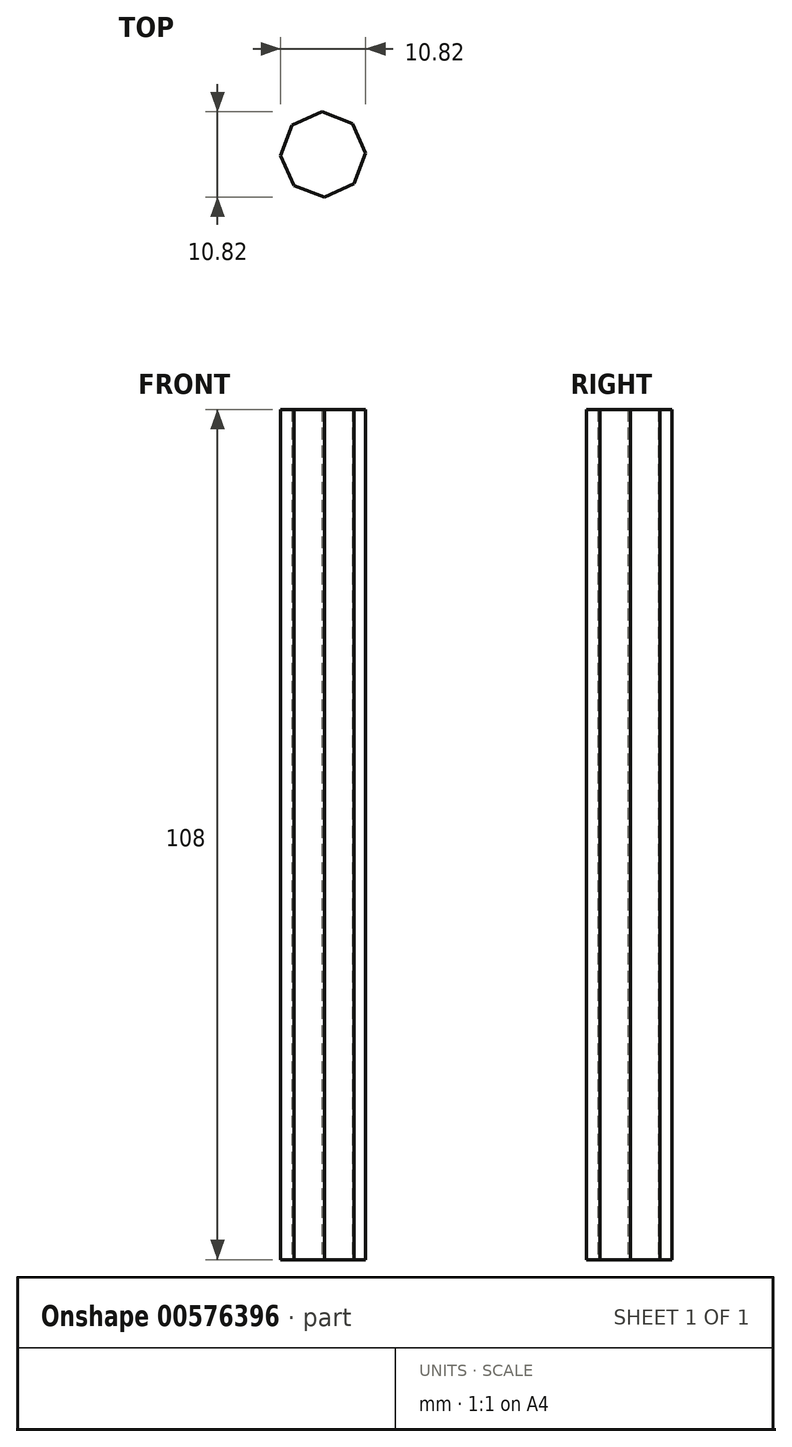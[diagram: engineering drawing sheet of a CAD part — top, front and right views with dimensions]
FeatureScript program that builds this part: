
annotation { "Feature Type Name" : "Feature", "Feature Type Description" : "" }
export const myFeature = defineFeature(function(context is Context, id is Id, definition is map)
    precondition{}
    {
        {
            var Q0;
            Q0=qCreatedBy(makeId("Top.planeOp"),FACE);
            var sketch = newSketch(context, id + "F0", { "sketchPlane" : qUnion([Q0])});
            skCircle(sketch, "E0.cCircle", {"center": v(0, 0) * mm, "radius": 5 * mm, "construction": true});
            skLineSegment(sketch, "E0.0", {"start": v(3.72, 3.93) * mm, "end": v(5.4, 0.15) * mm});
            skLineSegment(sketch, "E0.1", {"start": v(5.4, 0.15) * mm, "end": v(3.93, -3.72) * mm});
            skLineSegment(sketch, "E0.2", {"start": v(3.93, -3.72) * mm, "end": v(0.15, -5.4) * mm});
            skLineSegment(sketch, "E0.3", {"start": v(0.15, -5.4) * mm, "end": v(-3.72, -3.93) * mm});
            skLineSegment(sketch, "E0.4", {"start": v(-3.72, -3.93) * mm, "end": v(-5.4, -0.15) * mm});
            skLineSegment(sketch, "E0.5", {"start": v(-5.4, -0.15) * mm, "end": v(-3.93, 3.72) * mm});
            skLineSegment(sketch, "E0.6", {"start": v(-3.93, 3.72) * mm, "end": v(-0.15, 5.4) * mm});
            skLineSegment(sketch, "E0.7", {"start": v(-0.15, 5.4) * mm, "end": v(3.72, 3.93) * mm});
            skPoint(sketch, "E0.0.midPoint", {"position": v(4.56, 2.04) * mm});
            skSolve(sketch);
        }
        {
            var Q0;
            Q0=makeQuery(id+"F0.imprint","IMPRINT",FACE,{"disambiguationData":[TD([[makeQuery(id+"F0.imprint","IMPRINT",EDGE,{"derivedFrom":sQuery(id+"F0.wireOp",EDGE,"E0.0")}),-1.0]])]});
            extrude(context, id + "F1", {"entities" : qUnion([Q0]), "depth" : 108 * mm, "offsetDistance" : 25.4 * mm});
        }
    });
